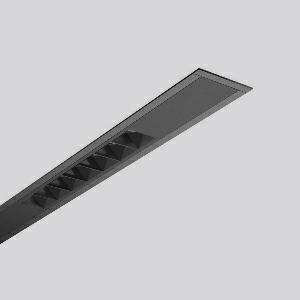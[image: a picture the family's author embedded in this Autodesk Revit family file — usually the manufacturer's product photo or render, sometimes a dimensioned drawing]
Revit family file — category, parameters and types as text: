
# Revit family: less_is_more_beamline_312472_003_1_b8b0
name_source: partatom
category: Lighting Fixtures
units: mm (PartAtom-declared; Revit-internal decimal feet)

## family parameters
Cut with Voids When Loaded = No
Host = Face
Light Source = No
Part Type = Normal
Room Calculation Point = No
Round Connector Dimension = Use Diameter
Shared = No

## types (1)
- LESS IS MORE BEAMLINE (1 x LED Modul 940, 1050 lm, 4000)
    Apparent Load = 35 VA
    CIE Flux Codes = 100 100 100 100 100
    Color Rendering = 92
    Color Temperature = 4000
    Default Elevation = 1800 mm
    Description = Series: LESS IS MORE BEAMLINE
Linear recessed ceiling and wall luminaire for aesthetically sophisticated lighting. Luminaire with three LED light units. Housing: extruded aluminium profile, powder-coated. End cap aluminium powder-coated. LED light unit with MRS technology: Mini-Reflector-System made of metallised thermoplastic with prismatic black glare-suppressing frame for pleasant glare-free light (RUG < 10). Each LED light unit has 7 reflector elements. Medium beam light distribution. Ceiling installation with pre-assembled SBS mounting system. LED unit with integrated converter interchangeable and removable. Suitable for through-wiring. 
Colour: deep black, matt (RAL 9005)
Length: 1702 mm
Width: 71 mm
Height: 1.5 mm
Cut-out length: 1688 mm
Cut-out width: 60 mm
Recess height: 125 mm
Luminaire: recess height: 106 mm
Lamp: LED
Socket: without socket
Colour temperature: 4000K
Colour rendering index (CRI): 90
System power: 35 W
Rated luminous flux: 3150 lm
Luminous efficiency: 90 lm/W
Control gear: Regulated power supply
Protection class: I
Type of protection: IP 20
    Height = 0 mm  [stored 0 ft]
    Lamp = 1 x LED Modul 940
    Lamp Light Flux = 1050 lm
    Lamp count = 1
    Length = 1702 mm
    Lifetime = 50000 h
    Luminous efficacy = 90 lm/W
    Manufacturer = RZB
    ModVariant = No
    Model = 312472.003.1
    Mounting Place = Ceiling, Wall
    Mounting Type = Recessed
    Number of Poles = 1
    OnlyDefault = Yes
    Power Factor = 1
    Product Name = LESS IS MORE BEAMLINE
    Product group = Recessed LED linear luminaires
    ProductGroupID = 407
    Protection Class = Protection class I
    Protection Degree = IP 20
    RLX_Detail_Level = 1
    RLX_Emergency_Light_Flux = 0 lm
    RLX_Emergency_Type = 0
    RLX_Emergency_Type_DB = No
    RlxData = <blob elided: 24173 chars, md5=c0cf273e>
    Socket = socket
    Standby Power = 0 W
    System Light Flux = 3150 lm
    System Power = 35 W
    Type Comments = Product without accessories
    Type Image = 312465.003.jpg
    URL = http://relux.com
    VarID = ---
    Voltage = 230 V
    Voltage Range = 220-240 V
    Weight = 0.00 kg
    Width = 71 mm

note: [stored X ft] marks values corroborated as IEEE doubles in the binary element streams (Revit-internal decimal feet)

## geometry (parser evidence)
native form markers: Blend x4, Sweep x18
no freeform markers — native parametric forms only
